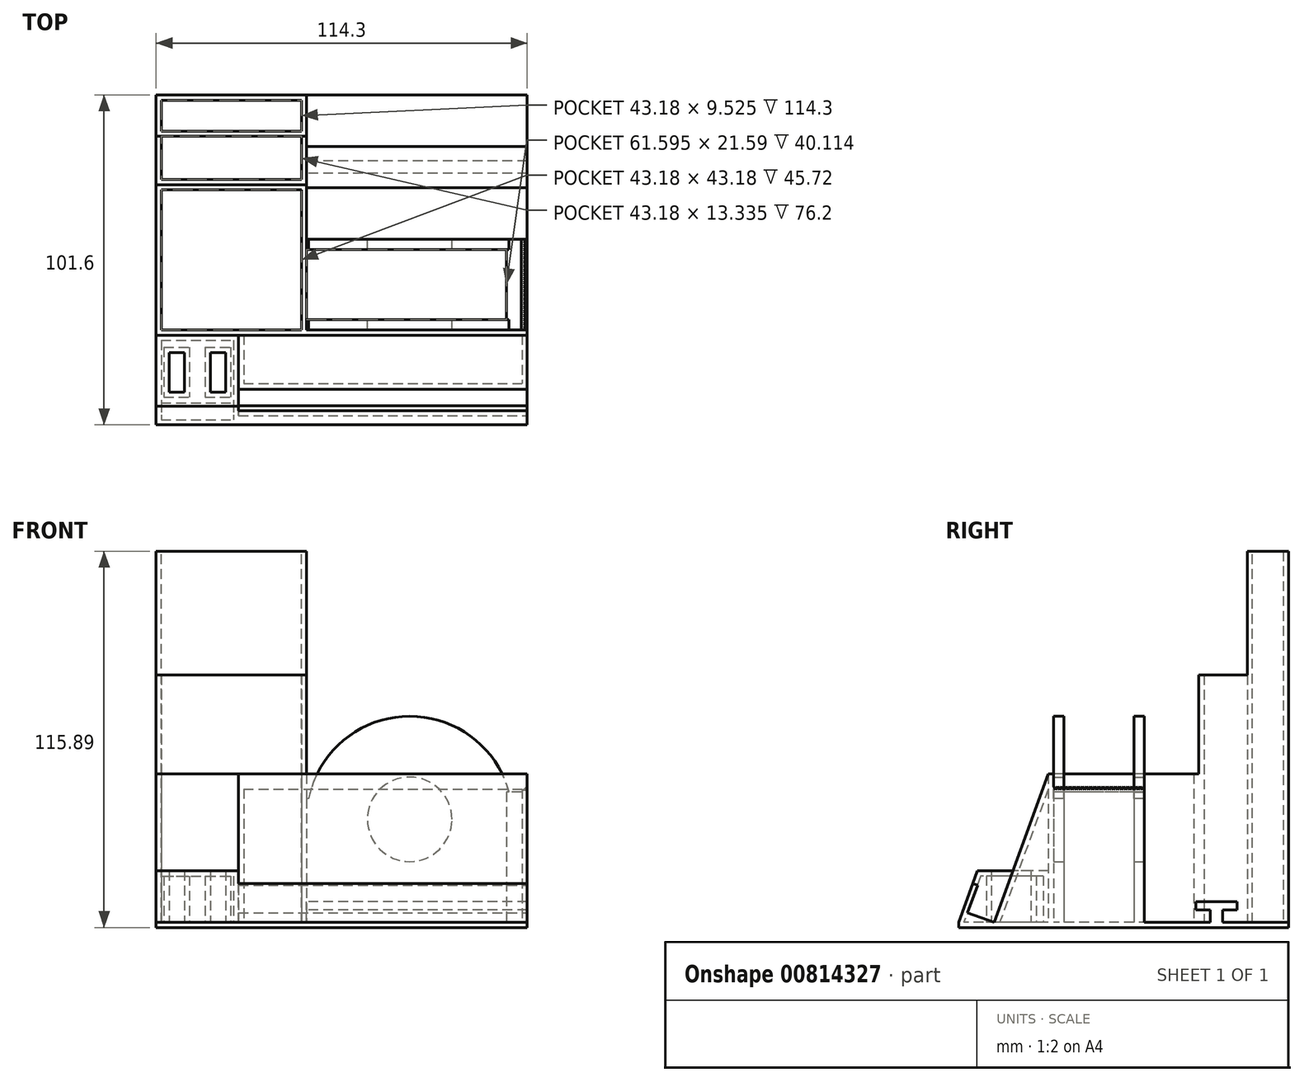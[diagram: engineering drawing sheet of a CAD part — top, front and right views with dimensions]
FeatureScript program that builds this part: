
annotation { "Feature Type Name" : "Feature", "Feature Type Description" : "" }
export const myFeature = defineFeature(function(context is Context, id is Id, definition is map)
    precondition{}
    {
        {
            var Q0;
            Q0=qCreatedBy(makeId("Top.planeOp"),FACE);
            var sketch = newSketch(context, id + "F0", { "sketchPlane" : qUnion([Q0])});
            skLineSegment(sketch, "E0.bottom", {"start": v(-57.15, 50.8) * mm, "end": v(57.15, 50.8) * mm});
            skLineSegment(sketch, "E0.top", {"start": v(-57.15, -50.8) * mm, "end": v(57.15, -50.8) * mm});
            skLineSegment(sketch, "E0.left", {"start": v(-57.15, 50.8) * mm, "end": v(-57.15, -50.8) * mm});
            skLineSegment(sketch, "E0.right", {"start": v(57.15, 50.8) * mm, "end": v(57.15, -50.8) * mm});
            skLineSegment(sketch, "E1", {"start": v(-57.15, 50.8) * mm, "end": v(57.15, -50.8) * mm, "construction": true});
            skSolve(sketch);
        }
        {
            var Q0;
            Q0 = qSketchRegion(id + "F0", true);
            extrude(context, id + "F1", {"entities" : qUnion([Q0]), "depth" : 1.59 * mm, "offsetDistance" : 25.4 * mm});
        }
        {
            var Q0;
            Q0=makeQuery(id+"F1.opExtrude","CAP_FACE",FACE,{"disambiguationData":[OSD([sQuery(id+"F0.wireOp",EDGE,"E0.bottom"),sQuery(id+"F0.wireOp",EDGE,"E0.top"),sQuery(id+"F0.wireOp",EDGE,"E0.left"),sQuery(id+"F0.wireOp",EDGE,"E0.right")])],"isStart":false});
            var sketch = newSketch(context, id + "F2", { "sketchPlane" : qUnion([Q0])});
            skLineSegment(sketch, "E2.bottom", {"start": v(-57.15, 23.18) * mm, "end": v(-10.8, 23.18) * mm});
            skLineSegment(sketch, "E2.top", {"start": v(-57.15, -23.18) * mm, "end": v(-10.8, -23.18) * mm});
            skLineSegment(sketch, "E2.left", {"start": v(-57.15, 23.18) * mm, "end": v(-57.15, -23.18) * mm});
            skLineSegment(sketch, "E2.right", {"start": v(-10.8, 23.18) * mm, "end": v(-10.8, -23.18) * mm});
            skLineSegment(sketch, "E3", {"start": v(0, 0) * mm, "end": v(-10.8, 0) * mm, "construction": true});
            skLineSegment(sketch, "E4.bottom", {"start": v(-55.56, 21.59) * mm, "end": v(-12.38, 21.59) * mm});
            skLineSegment(sketch, "E4.top", {"start": v(-55.56, -21.6) * mm, "end": v(-12.38, -21.6) * mm});
            skLineSegment(sketch, "E4.left", {"start": v(-55.56, 21.59) * mm, "end": v(-55.56, -21.6) * mm});
            skLineSegment(sketch, "E4.right", {"start": v(-12.38, 21.6) * mm, "end": v(-12.38, -21.6) * mm});
            skLineSegment(sketch, "E5", {"start": v(-57.15, 23.18) * mm, "end": v(-10.8, -23.18) * mm, "construction": true});
            skPoint(sketch, "E6", {"position": v(-33.97, 0) * mm});
            skLineSegment(sketch, "E7", {"start": v(-12.38, 21.6) * mm, "end": v(-55.56, -21.6) * mm, "construction": true});
            skSolve(sketch);
        }
        {
            var Q0;
            Q0 = qSketchRegion(id + "F2", true);
            extrude(context, id + "F3", {"entities" : qUnion([Q0]), "operationType" : NewBodyOperationType.ADD, "depth" : 45.72 * mm, "offsetDistance" : 25.4 * mm});
        }
        {
            var Q0;
            {var subQ0=sQuery(id+"F0.wireOp",EDGE,"E0.left");var subQ1=sQuery(id+"F0.wireOp",EDGE,"E0.top");var subQ2=sQuery(id+"F0.wireOp",EDGE,"E0.right");var subQ3=sQuery(id+"F0.wireOp",EDGE,"E0.bottom");Q0=makeQuery(id+"F3.boolean.opBoolean","SPLIT",FACE,{"disambiguationData":[TD([makeQuery(id+"F1.opExtrude","SWEPT_FACE",FACE,{"disambiguationData":[OSD([subQ3])]})])],"derivedFrom":makeQuery(id+"F1.opExtrude","CAP_FACE",FACE,{"disambiguationData":[OSD([subQ3,subQ1,subQ0,subQ2])],"isStart":false})});}
            var sketch = newSketch(context, id + "F4", { "sketchPlane" : qUnion([Q0])});
            skLineSegment(sketch, "E8.bottom", {"start": v(57.15, -21.6) * mm, "end": v(-31.75, -21.6) * mm});
            skLineSegment(sketch, "E8.top", {"start": v(57.15, -23.18) * mm, "end": v(-31.75, -23.18) * mm});
            skLineSegment(sketch, "E8.left", {"start": v(57.15, -21.6) * mm, "end": v(57.15, -23.18) * mm});
            skLineSegment(sketch, "E8.right", {"start": v(-31.75, -21.6) * mm, "end": v(-31.75, -23.18) * mm});
            skSolve(sketch);
        }
        {
            var Q0;
            Q0 = qSketchRegion(id + "F4", true);
            extrude(context, id + "F5", {"entities" : qUnion([Q0]), "operationType" : NewBodyOperationType.ADD, "depth" : 45.72 * mm, "offsetDistance" : 25.4 * mm});
        }
        {
            var Q0;
            Q0=makeQuery(id+"F5.boolean.opBoolean","MERGE",FACE,{"derivedFrom":[makeQuery(id+"F1.opExtrude","SWEPT_FACE",FACE,{"disambiguationData":[OSD([sQuery(id+"F0.wireOp",EDGE,"E0.right")])]}),makeQuery(id+"F5.opExtrude","SWEPT_FACE",FACE,{"disambiguationData":[OSD([sQuery(id+"F4.wireOp",EDGE,"E8.left")])]})]});
            var sketch = newSketch(context, id + "F6", { "sketchPlane" : qUnion([Q0])});
            skLineSegment(sketch, "E9", {"start": v(-50.8, 1.59) * mm, "end": v(-46.46, 13.52) * mm});
            skLineSegment(sketch, "E10", {"start": v(-46.46, 13.52) * mm, "end": v(-44.96, 12.98) * mm});
            skLineSegment(sketch, "E11", {"start": v(-44.96, 12.98) * mm, "end": v(-48.02, 4.57) * mm});
            skLineSegment(sketch, "E12", {"start": v(-48.02, 4.57) * mm, "end": v(-39.82, 1.59) * mm});
            skLineSegment(sketch, "E13", {"start": v(-39.82, 1.59) * mm, "end": v(-23.18, 47.3) * mm});
            skLineSegment(sketch, "E14", {"start": v(-23.18, 47.3) * mm, "end": v(-23.18, 42.67) * mm});
            skLineSegment(sketch, "E15", {"start": v(-23.18, 42.67) * mm, "end": v(-38.13, 1.59) * mm});
            skLineSegment(sketch, "E16", {"start": v(-50.8, 1.59) * mm, "end": v(-39.82, 1.59) * mm});
            skLineSegment(sketch, "E17", {"start": v(-39.82, 1.59) * mm, "end": v(-38.13, 1.59) * mm});
            skSolve(sketch);
        }
        {
            var Q0;
            Q0 = qSketchRegion(id + "F6", true);
            extrude(context, id + "F7", {"entities" : qUnion([Q0]), "operationType" : NewBodyOperationType.ADD, "oppositeDirection" : true, "depth" : 88.9 * mm, "offsetDistance" : 25.4 * mm});
        }
        {
            var Q0;
            Q0=makeQuery(id+"F7.boolean.opBoolean","MERGE",FACE,{"derivedFrom":[makeQuery(id+"F5.boolean.opBoolean","MERGE",FACE,{"derivedFrom":[makeQuery(id+"F1.opExtrude","SWEPT_FACE",FACE,{"disambiguationData":[OSD([sQuery(id+"F0.wireOp",EDGE,"E0.right")])]}),makeQuery(id+"F5.opExtrude","SWEPT_FACE",FACE,{"disambiguationData":[OSD([sQuery(id+"F4.wireOp",EDGE,"E8.left")])]})]}),makeQuery(id+"F7.opExtrude","CAP_FACE",FACE,{"disambiguationData":[OSD([sQuery(id+"F6.wireOp",EDGE,"E9"),sQuery(id+"F6.wireOp",EDGE,"E10"),sQuery(id+"F6.wireOp",EDGE,"E11"),sQuery(id+"F6.wireOp",EDGE,"E12"),sQuery(id+"F6.wireOp",EDGE,"E16")])],"isStart":true}),makeQuery(id+"F7.opExtrude","CAP_FACE",FACE,{"disambiguationData":[OSD([sQuery(id+"F6.wireOp",EDGE,"E13"),sQuery(id+"F6.wireOp",EDGE,"E14"),sQuery(id+"F6.wireOp",EDGE,"E15"),sQuery(id+"F6.wireOp",EDGE,"E17")])],"isStart":true})]});
            var sketch = newSketch(context, id + "F8", { "sketchPlane" : qUnion([Q0])});
            skLineSegment(sketch, "E18", {"start": v(-23.18, 42.67) * mm, "end": v(-38.13, 1.59) * mm});
            skLineSegment(sketch, "E19", {"start": v(-38.13, 1.59) * mm, "end": v(-23.18, 1.59) * mm});
            skLineSegment(sketch, "E20", {"start": v(-23.18, 1.59) * mm, "end": v(-23.18, 42.67) * mm});
            skSolve(sketch);
        }
        {
            var Q0;
            Q0 = qSketchRegion(id + "F8", true);
            extrude(context, id + "F9", {"entities" : qUnion([Q0]), "operationType" : NewBodyOperationType.ADD, "oppositeDirection" : true, "depth" : 1.59 * mm, "offsetDistance" : 25.4 * mm});
        }
        {
            var Q0;
            Q0=makeQuery(id+"F7.opExtrude","CAP_FACE",FACE,{"disambiguationData":[OSD([sQuery(id+"F6.wireOp",EDGE,"E13"),sQuery(id+"F6.wireOp",EDGE,"E14"),sQuery(id+"F6.wireOp",EDGE,"E15"),sQuery(id+"F6.wireOp",EDGE,"E17")])],"isStart":false});
            var sketch = newSketch(context, id + "F10", { "sketchPlane" : qUnion([Q0])});
            skLineSegment(sketch, "E21", {"start": v(38.13, 1.59) * mm, "end": v(23.18, 42.67) * mm});
            skLineSegment(sketch, "E22", {"start": v(23.18, 42.67) * mm, "end": v(23.18, 1.59) * mm});
            skLineSegment(sketch, "E23", {"start": v(23.18, 1.59) * mm, "end": v(38.13, 1.59) * mm});
            skSolve(sketch);
        }
        {
            var Q0;
            Q0 = qSketchRegion(id + "F10", true);
            extrude(context, id + "F11", {"entities" : qUnion([Q0]), "operationType" : NewBodyOperationType.ADD, "oppositeDirection" : true, "depth" : 1.59 * mm, "offsetDistance" : 25.4 * mm});
        }
        {
            var Q0;
            {var subQ5=sQuery(id+"F0.wireOp",EDGE,"E0.top");var subQ6=makeQuery(id+"F1.opExtrude","SWEPT_FACE",FACE,{"disambiguationData":[OSD([subQ5])]});var subQ7=sQuery(id+"F0.wireOp",EDGE,"E0.left");var subQ10=sQuery(id+"F0.wireOp",EDGE,"E0.right");var subQ12=sQuery(id+"F0.wireOp",EDGE,"E0.bottom");Q0=makeQuery(id+"F11.boolean.opBoolean","SPLIT",FACE,{"disambiguationData":[TD([subQ6])],"derivedFrom":makeQuery(id+"F5.boolean.opBoolean","SPLIT",FACE,{"disambiguationData":[TD([subQ6])],"derivedFrom":makeQuery(id+"F3.boolean.opBoolean","SPLIT",FACE,{"disambiguationData":[TD([makeQuery(id+"F1.opExtrude","SWEPT_FACE",FACE,{"disambiguationData":[OSD([subQ12])]})])],"derivedFrom":makeQuery(id+"F1.opExtrude","CAP_FACE",FACE,{"disambiguationData":[OSD([subQ12,subQ5,subQ7,subQ10])],"isStart":false})})})});}
            var sketch = newSketch(context, id + "F12", { "sketchPlane" : qUnion([Q0])});
            skLineSegment(sketch, "E24.bottom", {"start": v(-57.15, -23.18) * mm, "end": v(-31.75, -23.18) * mm});
            skLineSegment(sketch, "E24.top", {"start": v(-57.15, -50.8) * mm, "end": v(-31.75, -50.8) * mm});
            skLineSegment(sketch, "E24.left", {"start": v(-57.15, -23.18) * mm, "end": v(-57.15, -50.8) * mm});
            skLineSegment(sketch, "E24.right", {"start": v(-31.75, -23.18) * mm, "end": v(-31.75, -50.8) * mm});
            skLineSegment(sketch, "E25.bottom", {"start": v(-53.15, -28.51) * mm, "end": v(-48.45, -28.51) * mm});
            skLineSegment(sketch, "E25.top", {"start": v(-53.15, -40.7) * mm, "end": v(-48.45, -40.7) * mm});
            skLineSegment(sketch, "E25.left", {"start": v(-53.15, -28.51) * mm, "end": v(-53.15, -40.7) * mm});
            skLineSegment(sketch, "E25.right", {"start": v(-48.45, -28.51) * mm, "end": v(-48.45, -40.7) * mm});
            skLineSegment(sketch, "E26.bottom", {"start": v(-40.45, -28.51) * mm, "end": v(-35.75, -28.51) * mm});
            skLineSegment(sketch, "E26.top", {"start": v(-40.45, -40.7) * mm, "end": v(-35.75, -40.7) * mm});
            skLineSegment(sketch, "E26.left", {"start": v(-40.45, -28.51) * mm, "end": v(-40.45, -40.7) * mm});
            skLineSegment(sketch, "E26.right", {"start": v(-35.75, -28.51) * mm, "end": v(-35.75, -40.7) * mm});
            skLineSegment(sketch, "E27", {"start": v(-44.45, -34.6) * mm, "end": v(-40.45, -34.6) * mm, "construction": true});
            skLineSegment(sketch, "E28", {"start": v(-48.45, -34.6) * mm, "end": v(-44.45, -34.6) * mm, "construction": true});
            skLineSegment(sketch, "E29", {"start": v(-44.45, -34.6) * mm, "end": v(-44.45, -23.18) * mm, "construction": true});
            skLineSegment(sketch, "E30", {"start": v(-53.15, -34.6) * mm, "end": v(-57.15, -34.6) * mm, "construction": true});
            skLineSegment(sketch, "E31.bottom", {"start": v(-55.56, -24.77) * mm, "end": v(-33.34, -24.77) * mm});
            skLineSegment(sketch, "E31.top", {"start": v(-55.56, -49.21) * mm, "end": v(-33.34, -49.21) * mm});
            skLineSegment(sketch, "E31.left", {"start": v(-55.56, -24.77) * mm, "end": v(-55.56, -49.21) * mm});
            skLineSegment(sketch, "E31.right", {"start": v(-33.34, -24.77) * mm, "end": v(-33.34, -49.21) * mm});
            skLineSegment(sketch, "E32.bottom", {"start": v(-42.04, -26.92) * mm, "end": v(-34.16, -26.92) * mm});
            skLineSegment(sketch, "E32.top", {"start": v(-42.04, -42.3) * mm, "end": v(-34.16, -42.3) * mm});
            skLineSegment(sketch, "E32.left", {"start": v(-42.04, -26.92) * mm, "end": v(-42.04, -42.3) * mm});
            skLineSegment(sketch, "E32.right", {"start": v(-34.16, -26.92) * mm, "end": v(-34.16, -42.3) * mm});
            skLineSegment(sketch, "E33.bottom", {"start": v(-54.74, -26.92) * mm, "end": v(-46.86, -26.92) * mm});
            skLineSegment(sketch, "E33.top", {"start": v(-54.74, -42.3) * mm, "end": v(-46.86, -42.3) * mm});
            skLineSegment(sketch, "E33.left", {"start": v(-54.74, -26.92) * mm, "end": v(-54.74, -42.3) * mm});
            skLineSegment(sketch, "E33.right", {"start": v(-46.86, -26.92) * mm, "end": v(-46.86, -42.3) * mm});
            skSolve(sketch);
        }
        {
            var Q0;
            Q0 = qSketchRegion(id + "F12", true);
            var Q1;
            Q1=makeQuery(id+"F12.imprint","IMPRINT",FACE,{"disambiguationData":[TD([[makeQuery(id+"F12.imprint","IMPRINT",EDGE,{"derivedFrom":sQuery(id+"F12.wireOp",EDGE,"E26.bottom")}),1.0]])]});
            var Q2;
            Q2=makeQuery(id+"F12.imprint","IMPRINT",FACE,{"disambiguationData":[TD([[makeQuery(id+"F12.imprint","IMPRINT",EDGE,{"derivedFrom":sQuery(id+"F12.wireOp",EDGE,"E25.bottom")}),1.0]])]});
            extrude(context, id + "F13", {"entities" : qUnion([Q0, Q1, Q2]), "operationType" : NewBodyOperationType.ADD, "depth" : 15.88 * mm, "offsetDistance" : 25.4 * mm});
        }
        {
            var Q0;
            Q0=makeQuery(id+"F13.opExtrude","CAP_FACE",FACE,{"disambiguationData":[OSD([sQuery(id+"F12.wireOp",EDGE,"E24.bottom"),sQuery(id+"F12.wireOp",EDGE,"E24.top"),sQuery(id+"F12.wireOp",EDGE,"E24.left"),sQuery(id+"F12.wireOp",EDGE,"E24.right"),sQuery(id+"F12.wireOp",EDGE,"E31.bottom"),sQuery(id+"F12.wireOp",EDGE,"E31.top"),sQuery(id+"F12.wireOp",EDGE,"E31.left"),sQuery(id+"F12.wireOp",EDGE,"E31.right")])],"isStart":false});
            var sketch = newSketch(context, id + "F14", { "sketchPlane" : qUnion([Q0])});
            skLineSegment(sketch, "E34.bottom", {"start": v(-57.15, -23.18) * mm, "end": v(-31.75, -23.18) * mm});
            skLineSegment(sketch, "E34.top", {"start": v(-57.15, -50.8) * mm, "end": v(-31.75, -50.8) * mm});
            skLineSegment(sketch, "E34.left", {"start": v(-57.15, -23.18) * mm, "end": v(-57.15, -50.8) * mm});
            skLineSegment(sketch, "E34.right", {"start": v(-31.75, -23.18) * mm, "end": v(-31.75, -50.8) * mm});
            skLineSegment(sketch, "E35.bottom", {"start": v(-53.15, -28.51) * mm, "end": v(-48.45, -28.51) * mm});
            skLineSegment(sketch, "E35.top", {"start": v(-53.15, -40.7) * mm, "end": v(-48.45, -40.7) * mm});
            skLineSegment(sketch, "E35.left", {"start": v(-53.15, -28.51) * mm, "end": v(-53.15, -40.7) * mm});
            skLineSegment(sketch, "E35.right", {"start": v(-48.45, -28.51) * mm, "end": v(-48.45, -40.7) * mm});
            skLineSegment(sketch, "E36.bottom", {"start": v(-40.45, -28.51) * mm, "end": v(-35.75, -28.51) * mm});
            skLineSegment(sketch, "E36.top", {"start": v(-40.45, -40.7) * mm, "end": v(-35.75, -40.7) * mm});
            skLineSegment(sketch, "E36.left", {"start": v(-40.45, -28.51) * mm, "end": v(-40.45, -40.7) * mm});
            skLineSegment(sketch, "E36.right", {"start": v(-35.75, -28.51) * mm, "end": v(-35.75, -40.7) * mm});
            skSolve(sketch);
        }
        {
            var Q0;
            Q0 = qSketchRegion(id + "F14", true);
            extrude(context, id + "F15", {"entities" : qUnion([Q0]), "operationType" : NewBodyOperationType.ADD, "oppositeDirection" : true, "depth" : 1.59 * mm, "offsetDistance" : 25.4 * mm});
        }
        {
            var Q0;
            Q0=makeQuery(id+"F13.opExtrude","SWEPT_FACE",FACE,{"disambiguationData":[OSD([sQuery(id+"F12.wireOp",EDGE,"E24.right")])]});
            var sketch = newSketch(context, id + "F16", { "sketchPlane" : qUnion([Q0])});
            skLineSegment(sketch, "E37", {"start": v(-50.8, 1.59) * mm, "end": v(-45.02, 17.46) * mm});
            skLineSegment(sketch, "E38", {"start": v(-45.02, 17.46) * mm, "end": v(-50.8, 17.46) * mm});
            skLineSegment(sketch, "E39", {"start": v(-50.8, 17.46) * mm, "end": v(-50.8, 1.59) * mm});
            skSolve(sketch);
        }
        {
            var Q0;
            Q0 = qSketchRegion(id + "F16", true);
            extrude(context, id + "F17", {"entities" : qUnion([Q0]), "operationType" : NewBodyOperationType.REMOVE, "oppositeDirection" : true, "depth" : 25.4 * mm, "offsetDistance" : 25.4 * mm});
        }
        {
            var Q0;
            {var subQ1=sQuery(id+"F0.wireOp",EDGE,"E0.left");var subQ3=sQuery(id+"F0.wireOp",EDGE,"E0.right");var subQ6=sQuery(id+"F0.wireOp",EDGE,"E0.bottom");var subQ7=makeQuery(id+"F1.opExtrude","SWEPT_FACE",FACE,{"disambiguationData":[OSD([subQ6])]});var subQ9=sQuery(id+"F0.wireOp",EDGE,"E0.top");Q0=makeQuery(id+"F5.boolean.opBoolean","SPLIT",FACE,{"disambiguationData":[TD([subQ7])],"derivedFrom":makeQuery(id+"F3.boolean.opBoolean","SPLIT",FACE,{"disambiguationData":[TD([subQ7])],"derivedFrom":makeQuery(id+"F1.opExtrude","CAP_FACE",FACE,{"disambiguationData":[OSD([subQ6,subQ9,subQ1,subQ3])],"isStart":false})})});}
            var sketch = newSketch(context, id + "F18", { "sketchPlane" : qUnion([Q0])});
            skLineSegment(sketch, "E40.bottom", {"start": v(-10.8, -21.6) * mm, "end": v(57.15, -21.6) * mm});
            skLineSegment(sketch, "E40.top", {"start": v(-10.8, -18.42) * mm, "end": v(57.15, -18.42) * mm});
            skLineSegment(sketch, "E40.left", {"start": v(-10.8, -21.6) * mm, "end": v(-10.8, -18.42) * mm});
            skLineSegment(sketch, "E40.right", {"start": v(57.15, -21.6) * mm, "end": v(57.15, -18.42) * mm});
            skLineSegment(sketch, "E41.bottom", {"start": v(-10.8, 6.35) * mm, "end": v(57.15, 6.35) * mm});
            skLineSegment(sketch, "E41.top", {"start": v(-10.8, 3.17) * mm, "end": v(57.15, 3.17) * mm});
            skLineSegment(sketch, "E41.left", {"start": v(-10.8, 6.35) * mm, "end": v(-10.8, 3.17) * mm});
            skLineSegment(sketch, "E41.right", {"start": v(57.15, 6.35) * mm, "end": v(57.15, 3.17) * mm});
            skLineSegment(sketch, "E42.bottom", {"start": v(50.8, 3.17) * mm, "end": v(57.15, 3.17) * mm});
            skLineSegment(sketch, "E42.top", {"start": v(50.8, -18.42) * mm, "end": v(57.15, -18.42) * mm});
            skLineSegment(sketch, "E42.left", {"start": v(50.8, 3.17) * mm, "end": v(50.8, -18.42) * mm});
            skLineSegment(sketch, "E42.right", {"start": v(57.15, 3.17) * mm, "end": v(57.15, -18.42) * mm});
            skSolve(sketch);
        }
        {
            var Q0;
            Q0 = qSketchRegion(id + "F18", true);
            extrude(context, id + "F19", {"entities" : qUnion([Q0]), "operationType" : NewBodyOperationType.ADD, "depth" : 38.1 * mm, "offsetDistance" : 25.4 * mm});
        }
        {
            var Q0;
            Q0=makeQuery(id+"F5.opExtrude","SWEPT_FACE",FACE,{"disambiguationData":[OSD([sQuery(id+"F4.wireOp",EDGE,"E8.bottom")])]});
            var sketch = newSketch(context, id + "F20", { "sketchPlane" : qUnion([Q0])});
            skLineSegment(sketch, "E43", {"start": v(-57.15, 43.5) * mm, "end": v(-55.35, 41.7) * mm});
            skLineSegment(sketch, "E44", {"start": v(-55.35, 41.7) * mm, "end": v(-50.8, 41.7) * mm});
            skLineSegment(sketch, "E45", {"start": v(-50.8, 41.7) * mm, "end": v(-50.8, 39.69) * mm});
            skLineSegment(sketch, "E46", {"start": v(-50.8, 39.69) * mm, "end": v(-57.15, 39.69) * mm});
            skLineSegment(sketch, "E47", {"start": v(-57.15, 39.69) * mm, "end": v(-57.15, 43.5) * mm});
            skSolve(sketch);
        }
        {
            var Q0;
            Q0 = qSketchRegion(id + "F20", true);
            var Q1;
            Q1=makeQuery(id+"F19.opExtrude","SWEPT_FACE",FACE,{"disambiguationData":[OSD([sQuery(id+"F18.wireOp",EDGE,"E41.bottom")])]});
            extrude(context, id + "F21", {"entities" : qUnion([Q0]), "operationType" : NewBodyOperationType.ADD, "endBound" : BoundingType.UP_TO_SURFACE, "depth" : 25.4 * mm, "endBoundEntityFace" : qUnion([Q1]), "offsetDistance" : 25.4 * mm});
        }
        {
            var Q0;
            Q0=makeQuery(id+"F21.boolean.opBoolean","MERGE",FACE,{"derivedFrom":[makeQuery(id+"F19.boolean.opBoolean","MERGE",FACE,{"derivedFrom":[makeQuery(id+"F9.boolean.opBoolean","MERGE",FACE,{"derivedFrom":[makeQuery(id+"F7.boolean.opBoolean","MERGE",FACE,{"derivedFrom":[makeQuery(id+"F5.boolean.opBoolean","MERGE",FACE,{"derivedFrom":[makeQuery(id+"F1.opExtrude","SWEPT_FACE",FACE,{"disambiguationData":[OSD([sQuery(id+"F0.wireOp",EDGE,"E0.right")])]}),makeQuery(id+"F5.opExtrude","SWEPT_FACE",FACE,{"disambiguationData":[OSD([sQuery(id+"F4.wireOp",EDGE,"E8.left")])]})]}),makeQuery(id+"F7.opExtrude","CAP_FACE",FACE,{"disambiguationData":[OSD([sQuery(id+"F6.wireOp",EDGE,"E9"),sQuery(id+"F6.wireOp",EDGE,"E10"),sQuery(id+"F6.wireOp",EDGE,"E11"),sQuery(id+"F6.wireOp",EDGE,"E12"),sQuery(id+"F6.wireOp",EDGE,"E16")])],"isStart":true}),makeQuery(id+"F7.opExtrude","CAP_FACE",FACE,{"disambiguationData":[OSD([sQuery(id+"F6.wireOp",EDGE,"E13"),sQuery(id+"F6.wireOp",EDGE,"E14"),sQuery(id+"F6.wireOp",EDGE,"E15"),sQuery(id+"F6.wireOp",EDGE,"E17")])],"isStart":true})]}),makeQuery(id+"F9.opExtrude","CAP_FACE",FACE,{"disambiguationData":[OSD([sQuery(id+"F8.wireOp",EDGE,"E18"),sQuery(id+"F8.wireOp",EDGE,"E19"),sQuery(id+"F8.wireOp",EDGE,"E20")])],"isStart":true})]}),makeQuery(id+"F19.opExtrude","SWEPT_FACE",FACE,{"disambiguationData":[OSD([sQuery(id+"F18.wireOp",EDGE,"E40.right"),sQuery(id+"F18.wireOp",EDGE,"E41.right"),sQuery(id+"F18.wireOp",EDGE,"E42.right")])]})]}),makeQuery(id+"F21.opExtrude","SWEPT_FACE",FACE,{"disambiguationData":[OSD([sQuery(id+"F20.wireOp",EDGE,"E47")])]})]});
            var sketch = newSketch(context, id + "F22", { "sketchPlane" : qUnion([Q0])});
            skLineSegment(sketch, "E48", {"start": v(-21.6, 43.5) * mm, "end": v(-20.96, 42.4) * mm});
            skLineSegment(sketch, "E49", {"start": v(-20.96, 42.4) * mm, "end": v(-20.32, 43.5) * mm});
            skLineSegment(sketch, "E50", {"start": v(-20.32, 43.5) * mm, "end": v(-21.59, 43.5) * mm});
            skLineSegment(sketch, "E51.1.0.0", {"start": v(-19.05, 43.5) * mm, "end": v(-20.32, 43.5) * mm});
            skLineSegment(sketch, "E51.1.0.1", {"start": v(-19.69, 42.4) * mm, "end": v(-19.05, 43.5) * mm});
            skLineSegment(sketch, "E51.1.0.2", {"start": v(-20.32, 43.5) * mm, "end": v(-19.69, 42.4) * mm});
            skLineSegment(sketch, "E51.2.0.0", {"start": v(-17.78, 43.5) * mm, "end": v(-19.05, 43.5) * mm});
            skLineSegment(sketch, "E51.2.0.1", {"start": v(-18.42, 42.4) * mm, "end": v(-17.78, 43.5) * mm});
            skLineSegment(sketch, "E51.2.0.2", {"start": v(-19.05, 43.5) * mm, "end": v(-18.41, 42.4) * mm});
            skLineSegment(sketch, "E51.3.0.0", {"start": v(-16.51, 43.5) * mm, "end": v(-17.78, 43.5) * mm});
            skLineSegment(sketch, "E51.3.0.1", {"start": v(-17.15, 42.4) * mm, "end": v(-16.51, 43.5) * mm});
            skLineSegment(sketch, "E51.3.0.2", {"start": v(-17.78, 43.5) * mm, "end": v(-17.14, 42.4) * mm});
            skLineSegment(sketch, "E51.4.0.0", {"start": v(-15.24, 43.5) * mm, "end": v(-16.51, 43.5) * mm});
            skLineSegment(sketch, "E51.4.0.1", {"start": v(-15.88, 42.4) * mm, "end": v(-15.24, 43.5) * mm});
            skLineSegment(sketch, "E51.4.0.2", {"start": v(-16.51, 43.5) * mm, "end": v(-15.88, 42.4) * mm});
            skLineSegment(sketch, "E51.5.0.0", {"start": v(-13.97, 43.5) * mm, "end": v(-15.24, 43.5) * mm});
            skLineSegment(sketch, "E51.5.0.1", {"start": v(-14.6, 42.4) * mm, "end": v(-13.97, 43.5) * mm});
            skLineSegment(sketch, "E51.5.0.2", {"start": v(-15.24, 43.5) * mm, "end": v(-14.6, 42.4) * mm});
            skLineSegment(sketch, "E51.6.0.0", {"start": v(-12.7, 43.5) * mm, "end": v(-13.97, 43.5) * mm});
            skLineSegment(sketch, "E51.6.0.1", {"start": v(-13.34, 42.4) * mm, "end": v(-12.7, 43.5) * mm});
            skLineSegment(sketch, "E51.6.0.2", {"start": v(-13.97, 43.5) * mm, "end": v(-13.34, 42.4) * mm});
            skLineSegment(sketch, "E51.7.0.0", {"start": v(-11.43, 43.5) * mm, "end": v(-12.7, 43.5) * mm});
            skLineSegment(sketch, "E51.7.0.1", {"start": v(-12.07, 42.4) * mm, "end": v(-11.43, 43.5) * mm});
            skLineSegment(sketch, "E51.7.0.2", {"start": v(-12.7, 43.5) * mm, "end": v(-12.07, 42.4) * mm});
            skLineSegment(sketch, "E51.8.0.0", {"start": v(-10.16, 43.5) * mm, "end": v(-11.43, 43.5) * mm});
            skLineSegment(sketch, "E51.8.0.1", {"start": v(-10.8, 42.4) * mm, "end": v(-10.16, 43.5) * mm});
            skLineSegment(sketch, "E51.8.0.2", {"start": v(-11.43, 43.5) * mm, "end": v(-10.8, 42.4) * mm});
            skLineSegment(sketch, "E51.9.0.0", {"start": v(-8.89, 43.5) * mm, "end": v(-10.16, 43.5) * mm});
            skLineSegment(sketch, "E51.9.0.1", {"start": v(-9.53, 42.4) * mm, "end": v(-8.9, 43.5) * mm});
            skLineSegment(sketch, "E51.9.0.2", {"start": v(-10.16, 43.5) * mm, "end": v(-9.53, 42.4) * mm});
            skLineSegment(sketch, "E51.10.0.0", {"start": v(-7.62, 43.5) * mm, "end": v(-8.89, 43.5) * mm});
            skLineSegment(sketch, "E51.10.0.1", {"start": v(-8.26, 42.4) * mm, "end": v(-7.62, 43.5) * mm});
            skLineSegment(sketch, "E51.10.0.2", {"start": v(-8.9, 43.5) * mm, "end": v(-8.26, 42.4) * mm});
            skLineSegment(sketch, "E51.11.0.0", {"start": v(-6.35, 43.5) * mm, "end": v(-7.62, 43.5) * mm});
            skLineSegment(sketch, "E51.11.0.1", {"start": v(-6.99, 42.4) * mm, "end": v(-6.35, 43.5) * mm});
            skLineSegment(sketch, "E51.11.0.2", {"start": v(-7.62, 43.5) * mm, "end": v(-6.99, 42.4) * mm});
            skLineSegment(sketch, "E51.12.0.0", {"start": v(-5.08, 43.5) * mm, "end": v(-6.35, 43.5) * mm});
            skLineSegment(sketch, "E51.12.0.1", {"start": v(-5.72, 42.4) * mm, "end": v(-5.08, 43.5) * mm});
            skLineSegment(sketch, "E51.12.0.2", {"start": v(-6.35, 43.5) * mm, "end": v(-5.71, 42.4) * mm});
            skLineSegment(sketch, "E51.13.0.0", {"start": v(-3.8, 43.5) * mm, "end": v(-5.08, 43.5) * mm});
            skLineSegment(sketch, "E51.13.0.1", {"start": v(-4.45, 42.4) * mm, "end": v(-3.81, 43.5) * mm});
            skLineSegment(sketch, "E51.13.0.2", {"start": v(-5.08, 43.5) * mm, "end": v(-4.44, 42.4) * mm});
            skLineSegment(sketch, "E51.14.0.0", {"start": v(-2.54, 43.5) * mm, "end": v(-3.8, 43.5) * mm});
            skLineSegment(sketch, "E51.14.0.1", {"start": v(-3.18, 42.4) * mm, "end": v(-2.54, 43.5) * mm});
            skLineSegment(sketch, "E51.14.0.2", {"start": v(-3.8, 43.5) * mm, "end": v(-3.17, 42.4) * mm});
            skLineSegment(sketch, "E51.15.0.0", {"start": v(-1.27, 43.5) * mm, "end": v(-2.54, 43.5) * mm});
            skLineSegment(sketch, "E51.15.0.1", {"start": v(-1.9, 42.4) * mm, "end": v(-1.27, 43.5) * mm});
            skLineSegment(sketch, "E51.15.0.2", {"start": v(-2.54, 43.5) * mm, "end": v(-1.9, 42.4) * mm});
            skLineSegment(sketch, "E51.16.0.0", {"start": v(0, 43.5) * mm, "end": v(-1.27, 43.5) * mm});
            skLineSegment(sketch, "E51.16.0.1", {"start": v(-0.64, 42.4) * mm, "end": v(0, 43.5) * mm});
            skLineSegment(sketch, "E51.16.0.2", {"start": v(-1.27, 43.5) * mm, "end": v(-0.63, 42.4) * mm});
            skLineSegment(sketch, "E51.17.0.0", {"start": v(1.27, 43.5) * mm, "end": v(0, 43.5) * mm});
            skLineSegment(sketch, "E51.17.0.1", {"start": v(0.63, 42.4) * mm, "end": v(1.27, 43.5) * mm});
            skLineSegment(sketch, "E51.17.0.2", {"start": v(0, 43.5) * mm, "end": v(0.64, 42.4) * mm});
            skLineSegment(sketch, "E51.18.0.0", {"start": v(2.54, 43.5) * mm, "end": v(1.27, 43.5) * mm});
            skLineSegment(sketch, "E51.18.0.1", {"start": v(1.9, 42.4) * mm, "end": v(2.54, 43.5) * mm});
            skLineSegment(sketch, "E51.18.0.2", {"start": v(1.27, 43.5) * mm, "end": v(1.9, 42.4) * mm});
            skLineSegment(sketch, "E51.19.0.0", {"start": v(3.81, 43.5) * mm, "end": v(2.54, 43.5) * mm});
            skLineSegment(sketch, "E51.19.0.1", {"start": v(3.18, 42.4) * mm, "end": v(3.81, 43.5) * mm});
            skLineSegment(sketch, "E51.19.0.2", {"start": v(2.54, 43.5) * mm, "end": v(3.18, 42.4) * mm});
            skLineSegment(sketch, "E51.20.0.0", {"start": v(5.08, 43.5) * mm, "end": v(3.81, 43.5) * mm});
            skLineSegment(sketch, "E51.20.0.1", {"start": v(4.45, 42.4) * mm, "end": v(5.08, 43.5) * mm});
            skLineSegment(sketch, "E51.20.0.2", {"start": v(3.81, 43.5) * mm, "end": v(4.45, 42.4) * mm});
            skLineSegment(sketch, "E51.21.0.0", {"start": v(6.35, 43.5) * mm, "end": v(5.08, 43.5) * mm});
            skLineSegment(sketch, "E51.21.0.1", {"start": v(5.72, 42.4) * mm, "end": v(6.35, 43.5) * mm});
            skLineSegment(sketch, "E51.21.0.2", {"start": v(5.08, 43.5) * mm, "end": v(5.72, 42.4) * mm});
            skLineSegment(sketch, "E51.direction1", {"start": v(-20.96, 42.4) * mm, "end": v(-19.69, 42.4) * mm, "construction": true});
            skSolve(sketch);
        }
        {
            var Q0;
            Q0 = qSketchRegion(id + "F22", true);
            extrude(context, id + "F23", {"entities" : qUnion([Q0]), "operationType" : NewBodyOperationType.REMOVE, "oppositeDirection" : true, "depth" : 25.4 * mm, "offsetDistance" : 25.4 * mm});
        }
        {
            var Q0;
            {var subQ0=sQuery(id+"F18.wireOp",EDGE,"E41.bottom");Q0=makeQuery(id+"F21.boolean.opBoolean","MERGE",FACE,{"derivedFrom":[makeQuery(id+"F19.opExtrude","SWEPT_FACE",FACE,{"disambiguationData":[OSD([subQ0])]}),makeQuery(id+"F21.opExtrude","CAP_FACE",FACE,{"disambiguationData":[OSD([subQ0])],"isStart":false})]});}
            var sketch = newSketch(context, id + "F24", { "sketchPlane" : qUnion([Q0])});
            skArc(sketch, "E52", {"start": v(10.15, 39.69) * mm, "mid": v(-20.95, 65.09) * mm, "end": v(-52.06, 39.69) * mm});
            skLineSegment(sketch, "E53", {"start": v(10.15, 39.69) * mm, "end": v(-52.06, 39.69) * mm});
            skSolve(sketch);
        }
        {
            var Q0;
            Q0 = qSketchRegion(id + "F24", true);
            extrude(context, id + "F25", {"entities" : qUnion([Q0]), "operationType" : NewBodyOperationType.ADD, "oppositeDirection" : true, "depth" : 3.17 * mm, "offsetDistance" : 25.4 * mm});
        }
        {
            var Q0;
            Q0=makeQuery(id+"F5.opExtrude","SWEPT_FACE",FACE,{"disambiguationData":[OSD([sQuery(id+"F4.wireOp",EDGE,"E8.bottom")])]});
            var sketch = newSketch(context, id + "F26", { "sketchPlane" : qUnion([Q0])});
            skCircle(sketch, "E54", {"center": v(-20.95, 33.34) * mm, "radius": 31.75 * mm});
            skSolve(sketch);
        }
        {
            var Q0;
            Q0 = qSketchRegion(id + "F26", true);
            extrude(context, id + "F27", {"entities" : qUnion([Q0]), "operationType" : NewBodyOperationType.ADD, "depth" : 3.17 * mm, "offsetDistance" : 25.4 * mm});
        }
        {
            var Q0;
            {var subQ0=sQuery(id+"F18.wireOp",EDGE,"E41.bottom");Q0=makeQuery(id+"F25.boolean.opBoolean","MERGE",FACE,{"derivedFrom":[makeQuery(id+"F21.boolean.opBoolean","MERGE",FACE,{"derivedFrom":[makeQuery(id+"F19.opExtrude","SWEPT_FACE",FACE,{"disambiguationData":[OSD([subQ0])]}),makeQuery(id+"F21.opExtrude","CAP_FACE",FACE,{"disambiguationData":[OSD([subQ0])],"isStart":false})]}),makeQuery(id+"F25.opExtrude","CAP_FACE",FACE,{"disambiguationData":[OSD([sQuery(id+"F24.wireOp",EDGE,"E52"),sQuery(id+"F24.wireOp",EDGE,"E53")])],"isStart":true})]});}
            var sketch = newSketch(context, id + "F28", { "sketchPlane" : qUnion([Q0])});
            skCircle(sketch, "E55", {"center": v(-20.95, 33.34) * mm, "radius": 13.02 * mm});
            skSolve(sketch);
        }
        {
            var Q0;
            Q0 = qSketchRegion(id + "F28", true);
            extrude(context, id + "F29", {"entities" : qUnion([Q0]), "operationType" : NewBodyOperationType.REMOVE, "oppositeDirection" : true, "depth" : 27.94 * mm, "offsetDistance" : 25.4 * mm});
        }
        {
            var Q0;
            {var subQ2=sQuery(id+"F0.wireOp",EDGE,"E0.bottom");var subQ3=makeQuery(id+"F1.opExtrude","SWEPT_FACE",FACE,{"disambiguationData":[OSD([subQ2])]});var subQ5=sQuery(id+"F0.wireOp",EDGE,"E0.right");var subQ7=sQuery(id+"F0.wireOp",EDGE,"E0.left");var subQ10=sQuery(id+"F0.wireOp",EDGE,"E0.top");Q0=makeQuery(id+"F19.boolean.opBoolean","SPLIT",FACE,{"disambiguationData":[TD([subQ3])],"derivedFrom":makeQuery(id+"F5.boolean.opBoolean","SPLIT",FACE,{"disambiguationData":[TD([subQ3])],"derivedFrom":makeQuery(id+"F3.boolean.opBoolean","SPLIT",FACE,{"disambiguationData":[TD([subQ3])],"derivedFrom":makeQuery(id+"F1.opExtrude","CAP_FACE",FACE,{"disambiguationData":[OSD([subQ2,subQ10,subQ7,subQ5])],"isStart":false})})})});}
            var sketch = newSketch(context, id + "F30", { "sketchPlane" : qUnion([Q0])});
            skLineSegment(sketch, "E56.bottom", {"start": v(-57.15, 50.8) * mm, "end": v(-10.8, 50.8) * mm});
            skLineSegment(sketch, "E56.top", {"start": v(-57.15, 23.18) * mm, "end": v(-10.8, 23.18) * mm});
            skLineSegment(sketch, "E56.left", {"start": v(-57.15, 50.8) * mm, "end": v(-57.15, 23.18) * mm});
            skLineSegment(sketch, "E56.right", {"start": v(-10.8, 50.8) * mm, "end": v(-10.8, 23.18) * mm});
            skLineSegment(sketch, "E57.0", {"start": v(-12.38, 49.21) * mm, "end": v(-12.38, 24.77) * mm});
            skLineSegment(sketch, "E57.1", {"start": v(-55.56, 49.21) * mm, "end": v(-12.38, 49.21) * mm});
            skLineSegment(sketch, "E57.2", {"start": v(-55.56, 49.21) * mm, "end": v(-55.56, 24.77) * mm});
            skLineSegment(sketch, "E57.3", {"start": v(-55.56, 24.77) * mm, "end": v(-12.38, 24.77) * mm});
            skSolve(sketch);
        }
        {
            var Q0;
            Q0 = qSketchRegion(id + "F30", true);
            extrude(context, id + "F31", {"entities" : qUnion([Q0]), "operationType" : NewBodyOperationType.ADD, "depth" : 76.2 * mm, "offsetDistance" : 25.4 * mm});
        }
        {
            var Q0;
            Q0=makeQuery(id+"F31.opExtrude","CAP_FACE",FACE,{"disambiguationData":[OSD([sQuery(id+"F30.wireOp",EDGE,"E56.bottom"),sQuery(id+"F30.wireOp",EDGE,"E56.top"),sQuery(id+"F30.wireOp",EDGE,"E56.left"),sQuery(id+"F30.wireOp",EDGE,"E56.right"),sQuery(id+"F30.wireOp",EDGE,"E57.0"),sQuery(id+"F30.wireOp",EDGE,"E57.1"),sQuery(id+"F30.wireOp",EDGE,"E57.2"),sQuery(id+"F30.wireOp",EDGE,"E57.3")])],"isStart":false});
            var sketch = newSketch(context, id + "F32", { "sketchPlane" : qUnion([Q0])});
            skLineSegment(sketch, "E58.bottom", {"start": v(-57.15, 50.8) * mm, "end": v(-10.8, 50.8) * mm});
            skLineSegment(sketch, "E58.top", {"start": v(-57.15, 38.1) * mm, "end": v(-10.8, 38.1) * mm});
            skLineSegment(sketch, "E58.left", {"start": v(-57.15, 50.8) * mm, "end": v(-57.15, 38.1) * mm});
            skLineSegment(sketch, "E58.right", {"start": v(-10.8, 50.8) * mm, "end": v(-10.8, 38.1) * mm});
            skSolve(sketch);
        }
        {
            var Q0;
            Q0 = qSketchRegion(id + "F32", true);
            extrude(context, id + "F33", {"entities" : qUnion([Q0]), "operationType" : NewBodyOperationType.ADD, "oppositeDirection" : true, "depth" : 1.59 * mm, "offsetDistance" : 25.4 * mm});
        }
        {
            var Q0;
            Q0=makeQuery(id+"F33.boolean.opBoolean","MERGE",FACE,{"derivedFrom":[makeQuery(id+"F31.opExtrude","CAP_FACE",FACE,{"disambiguationData":[OSD([sQuery(id+"F30.wireOp",EDGE,"E56.bottom"),sQuery(id+"F30.wireOp",EDGE,"E56.top"),sQuery(id+"F30.wireOp",EDGE,"E56.left"),sQuery(id+"F30.wireOp",EDGE,"E56.right"),sQuery(id+"F30.wireOp",EDGE,"E57.0"),sQuery(id+"F30.wireOp",EDGE,"E57.1"),sQuery(id+"F30.wireOp",EDGE,"E57.2"),sQuery(id+"F30.wireOp",EDGE,"E57.3")])],"isStart":false}),makeQuery(id+"F33.opExtrude","CAP_FACE",FACE,{"disambiguationData":[OSD([sQuery(id+"F32.wireOp",EDGE,"E58.bottom"),sQuery(id+"F32.wireOp",EDGE,"E58.top"),sQuery(id+"F32.wireOp",EDGE,"E58.left"),sQuery(id+"F32.wireOp",EDGE,"E58.right")])],"isStart":true})]});
            var sketch = newSketch(context, id + "F34", { "sketchPlane" : qUnion([Q0])});
            skLineSegment(sketch, "E59.bottom", {"start": v(-55.56, 38.1) * mm, "end": v(-12.38, 38.1) * mm});
            skLineSegment(sketch, "E59.top", {"start": v(-55.56, 39.69) * mm, "end": v(-12.38, 39.69) * mm});
            skLineSegment(sketch, "E59.left", {"start": v(-55.56, 38.1) * mm, "end": v(-55.56, 39.69) * mm});
            skLineSegment(sketch, "E59.right", {"start": v(-12.38, 38.1) * mm, "end": v(-12.38, 39.69) * mm});
            skSolve(sketch);
        }
        {
            var Q0;
            Q0 = qSketchRegion(id + "F34", true);
            extrude(context, id + "F35", {"entities" : qUnion([Q0]), "operationType" : NewBodyOperationType.ADD, "oppositeDirection" : true, "depth" : 76.2 * mm, "offsetDistance" : 25.4 * mm});
        }
        {
            var Q0;
            Q0=makeQuery(id+"F33.boolean.opBoolean","MERGE",FACE,{"derivedFrom":[makeQuery(id+"F31.opExtrude","CAP_FACE",FACE,{"disambiguationData":[OSD([sQuery(id+"F30.wireOp",EDGE,"E56.bottom"),sQuery(id+"F30.wireOp",EDGE,"E56.top"),sQuery(id+"F30.wireOp",EDGE,"E56.left"),sQuery(id+"F30.wireOp",EDGE,"E56.right"),sQuery(id+"F30.wireOp",EDGE,"E57.0"),sQuery(id+"F30.wireOp",EDGE,"E57.1"),sQuery(id+"F30.wireOp",EDGE,"E57.2"),sQuery(id+"F30.wireOp",EDGE,"E57.3")])],"isStart":false}),makeQuery(id+"F33.opExtrude","CAP_FACE",FACE,{"disambiguationData":[OSD([sQuery(id+"F32.wireOp",EDGE,"E58.bottom"),sQuery(id+"F32.wireOp",EDGE,"E58.top"),sQuery(id+"F32.wireOp",EDGE,"E58.left"),sQuery(id+"F32.wireOp",EDGE,"E58.right")])],"isStart":true})]});
            var sketch = newSketch(context, id + "F36", { "sketchPlane" : qUnion([Q0])});
            skLineSegment(sketch, "E60.bottom", {"start": v(-57.15, 50.8) * mm, "end": v(-10.8, 50.8) * mm});
            skLineSegment(sketch, "E60.top", {"start": v(-57.15, 38.1) * mm, "end": v(-10.8, 38.1) * mm});
            skLineSegment(sketch, "E60.left", {"start": v(-57.15, 50.8) * mm, "end": v(-57.15, 38.1) * mm});
            skLineSegment(sketch, "E60.right", {"start": v(-10.8, 50.8) * mm, "end": v(-10.8, 38.1) * mm});
            skLineSegment(sketch, "E61.bottom", {"start": v(-55.56, 49.21) * mm, "end": v(-12.38, 49.21) * mm});
            skLineSegment(sketch, "E61.top", {"start": v(-55.56, 39.69) * mm, "end": v(-12.38, 39.69) * mm});
            skLineSegment(sketch, "E61.left", {"start": v(-55.56, 49.21) * mm, "end": v(-55.56, 39.69) * mm});
            skLineSegment(sketch, "E61.right", {"start": v(-12.38, 49.21) * mm, "end": v(-12.38, 39.69) * mm});
            skSolve(sketch);
        }
        {
            var Q0;
            Q0 = qSketchRegion(id + "F36", true);
            extrude(context, id + "F37", {"entities" : qUnion([Q0]), "operationType" : NewBodyOperationType.ADD, "depth" : 38.1 * mm, "offsetDistance" : 25.4 * mm});
        }
        {
            var Q0;
            Q0=makeQuery(id+"F37.boolean.opBoolean","SPLIT",FACE,{"disambiguationData":[TD([makeQuery(id+"F37.opExtrude","SWEPT_FACE",FACE,{"disambiguationData":[OSD([sQuery(id+"F36.wireOp",EDGE,"E61.bottom")])]})])],"derivedFrom":makeQuery(id+"F33.boolean.opBoolean","MERGE",FACE,{"derivedFrom":[makeQuery(id+"F31.opExtrude","CAP_FACE",FACE,{"disambiguationData":[OSD([sQuery(id+"F30.wireOp",EDGE,"E56.bottom"),sQuery(id+"F30.wireOp",EDGE,"E56.top"),sQuery(id+"F30.wireOp",EDGE,"E56.left"),sQuery(id+"F30.wireOp",EDGE,"E56.right"),sQuery(id+"F30.wireOp",EDGE,"E57.0"),sQuery(id+"F30.wireOp",EDGE,"E57.1"),sQuery(id+"F30.wireOp",EDGE,"E57.2"),sQuery(id+"F30.wireOp",EDGE,"E57.3")])],"isStart":false}),makeQuery(id+"F33.opExtrude","CAP_FACE",FACE,{"disambiguationData":[OSD([sQuery(id+"F32.wireOp",EDGE,"E58.bottom"),sQuery(id+"F32.wireOp",EDGE,"E58.top"),sQuery(id+"F32.wireOp",EDGE,"E58.left"),sQuery(id+"F32.wireOp",EDGE,"E58.right")])],"isStart":true})]})});
            var sketch = newSketch(context, id + "F38", { "sketchPlane" : qUnion([Q0])});
            skLineSegment(sketch, "E62.bottom", {"start": v(-55.56, 49.21) * mm, "end": v(-12.38, 49.21) * mm});
            skLineSegment(sketch, "E62.top", {"start": v(-55.56, 39.69) * mm, "end": v(-12.38, 39.69) * mm});
            skLineSegment(sketch, "E62.left", {"start": v(-55.56, 49.21) * mm, "end": v(-55.56, 39.69) * mm});
            skLineSegment(sketch, "E62.right", {"start": v(-12.38, 49.21) * mm, "end": v(-12.38, 39.69) * mm});
            skSolve(sketch);
        }
        {
            var Q0;
            Q0 = qSketchRegion(id + "F38", true);
            extrude(context, id + "F39", {"entities" : qUnion([Q0]), "operationType" : NewBodyOperationType.REMOVE, "oppositeDirection" : true, "depth" : 25.4 * mm, "offsetDistance" : 25.4 * mm});
        }
        {
            var Q0;
            Q0=makeQuery(id+"F37.boolean.opBoolean","MERGE",FACE,{"derivedFrom":[makeQuery(id+"F31.boolean.opBoolean","MERGE",FACE,{"derivedFrom":[makeQuery(id+"F3.opExtrude","SWEPT_FACE",FACE,{"disambiguationData":[OSD([sQuery(id+"F2.wireOp",EDGE,"E2.right")])]}),makeQuery(id+"F31.opExtrude","SWEPT_FACE",FACE,{"disambiguationData":[OSD([sQuery(id+"F30.wireOp",EDGE,"E56.right")])]})]}),makeQuery(id+"F37.opExtrude","SWEPT_FACE",FACE,{"disambiguationData":[OSD([sQuery(id+"F36.wireOp",EDGE,"E60.right")])]})]});
            var sketch = newSketch(context, id + "F40", { "sketchPlane" : qUnion([Q0])});
            skLineSegment(sketch, "E63", {"start": v(26.67, 1.59) * mm, "end": v(26.67, 5.4) * mm});
            skLineSegment(sketch, "E64", {"start": v(26.67, 5.4) * mm, "end": v(22.22, 5.4) * mm});
            skLineSegment(sketch, "E65", {"start": v(22.22, 5.4) * mm, "end": v(22.22, 7.94) * mm});
            skLineSegment(sketch, "E66", {"start": v(22.22, 7.94) * mm, "end": v(34.92, 7.94) * mm});
            skLineSegment(sketch, "E67", {"start": v(34.92, 7.94) * mm, "end": v(34.92, 5.4) * mm});
            skLineSegment(sketch, "E68", {"start": v(34.92, 5.4) * mm, "end": v(30.48, 5.4) * mm});
            skLineSegment(sketch, "E69", {"start": v(30.48, 5.4) * mm, "end": v(30.48, 1.59) * mm});
            skLineSegment(sketch, "E70", {"start": v(30.48, 1.59) * mm, "end": v(26.67, 1.59) * mm});
            skPoint(sketch, "E71", {"position": v(28.57, 1.59) * mm});
            skSolve(sketch);
        }
        {
            var Q0;
            Q0 = qSketchRegion(id + "F40", true);
            var Q1;
            Q1=makeQuery(id+"F21.boolean.opBoolean","MERGE",FACE,{"derivedFrom":[makeQuery(id+"F19.boolean.opBoolean","MERGE",FACE,{"derivedFrom":[makeQuery(id+"F9.boolean.opBoolean","MERGE",FACE,{"derivedFrom":[makeQuery(id+"F7.boolean.opBoolean","MERGE",FACE,{"derivedFrom":[makeQuery(id+"F5.boolean.opBoolean","MERGE",FACE,{"derivedFrom":[makeQuery(id+"F1.opExtrude","SWEPT_FACE",FACE,{"disambiguationData":[OSD([sQuery(id+"F0.wireOp",EDGE,"E0.right")])]}),makeQuery(id+"F5.opExtrude","SWEPT_FACE",FACE,{"disambiguationData":[OSD([sQuery(id+"F4.wireOp",EDGE,"E8.left")])]})]}),makeQuery(id+"F7.opExtrude","CAP_FACE",FACE,{"disambiguationData":[OSD([sQuery(id+"F6.wireOp",EDGE,"E9"),sQuery(id+"F6.wireOp",EDGE,"E10"),sQuery(id+"F6.wireOp",EDGE,"E11"),sQuery(id+"F6.wireOp",EDGE,"E12"),sQuery(id+"F6.wireOp",EDGE,"E16")])],"isStart":true}),makeQuery(id+"F7.opExtrude","CAP_FACE",FACE,{"disambiguationData":[OSD([sQuery(id+"F6.wireOp",EDGE,"E13"),sQuery(id+"F6.wireOp",EDGE,"E14"),sQuery(id+"F6.wireOp",EDGE,"E15"),sQuery(id+"F6.wireOp",EDGE,"E17")])],"isStart":true})]}),makeQuery(id+"F9.opExtrude","CAP_FACE",FACE,{"disambiguationData":[OSD([sQuery(id+"F8.wireOp",EDGE,"E18"),sQuery(id+"F8.wireOp",EDGE,"E19"),sQuery(id+"F8.wireOp",EDGE,"E20")])],"isStart":true})]}),makeQuery(id+"F19.opExtrude","SWEPT_FACE",FACE,{"disambiguationData":[OSD([sQuery(id+"F18.wireOp",EDGE,"E40.right"),sQuery(id+"F18.wireOp",EDGE,"E41.right"),sQuery(id+"F18.wireOp",EDGE,"E42.right")])]})]}),makeQuery(id+"F21.opExtrude","SWEPT_FACE",FACE,{"disambiguationData":[OSD([sQuery(id+"F20.wireOp",EDGE,"E47")])]})]});
            extrude(context, id + "F41", {"entities" : qUnion([Q0]), "operationType" : NewBodyOperationType.ADD, "endBound" : BoundingType.UP_TO_SURFACE, "depth" : 25.4 * mm, "endBoundEntityFace" : qUnion([Q1]), "offsetDistance" : 25.4 * mm});
        }
        {
            var Q0;
            Q0=makeQuery(id+"F13.opExtrude","SWEPT_FACE",FACE,{"disambiguationData":[OSD([sQuery(id+"F12.wireOp",EDGE,"E24.right")])]});
            var sketch = newSketch(context, id + "F42", { "sketchPlane" : qUnion([Q0])});
            skLineSegment(sketch, "E72", {"start": v(-45.02, 17.46) * mm, "end": v(-43.43, 17.46) * mm});
            skLineSegment(sketch, "E73", {"start": v(-43.43, 17.46) * mm, "end": v(-49.8, 0) * mm});
            skLineSegment(sketch, "E74", {"start": v(-49.8, 0) * mm, "end": v(-50.8, 0) * mm});
            skLineSegment(sketch, "E75", {"start": v(-50.8, 0) * mm, "end": v(-50.8, 1.59) * mm});
            skLineSegment(sketch, "E76", {"start": v(-50.8, 1.59) * mm, "end": v(-45.02, 17.46) * mm});
            skSolve(sketch);
        }
        {
            var Q0;
            Q0 = qSketchRegion(id + "F42", true);
            extrude(context, id + "F43", {"entities" : qUnion([Q0]), "operationType" : NewBodyOperationType.ADD, "oppositeDirection" : true, "depth" : 25.4 * mm, "offsetDistance" : 25.4 * mm});
        }
    });
